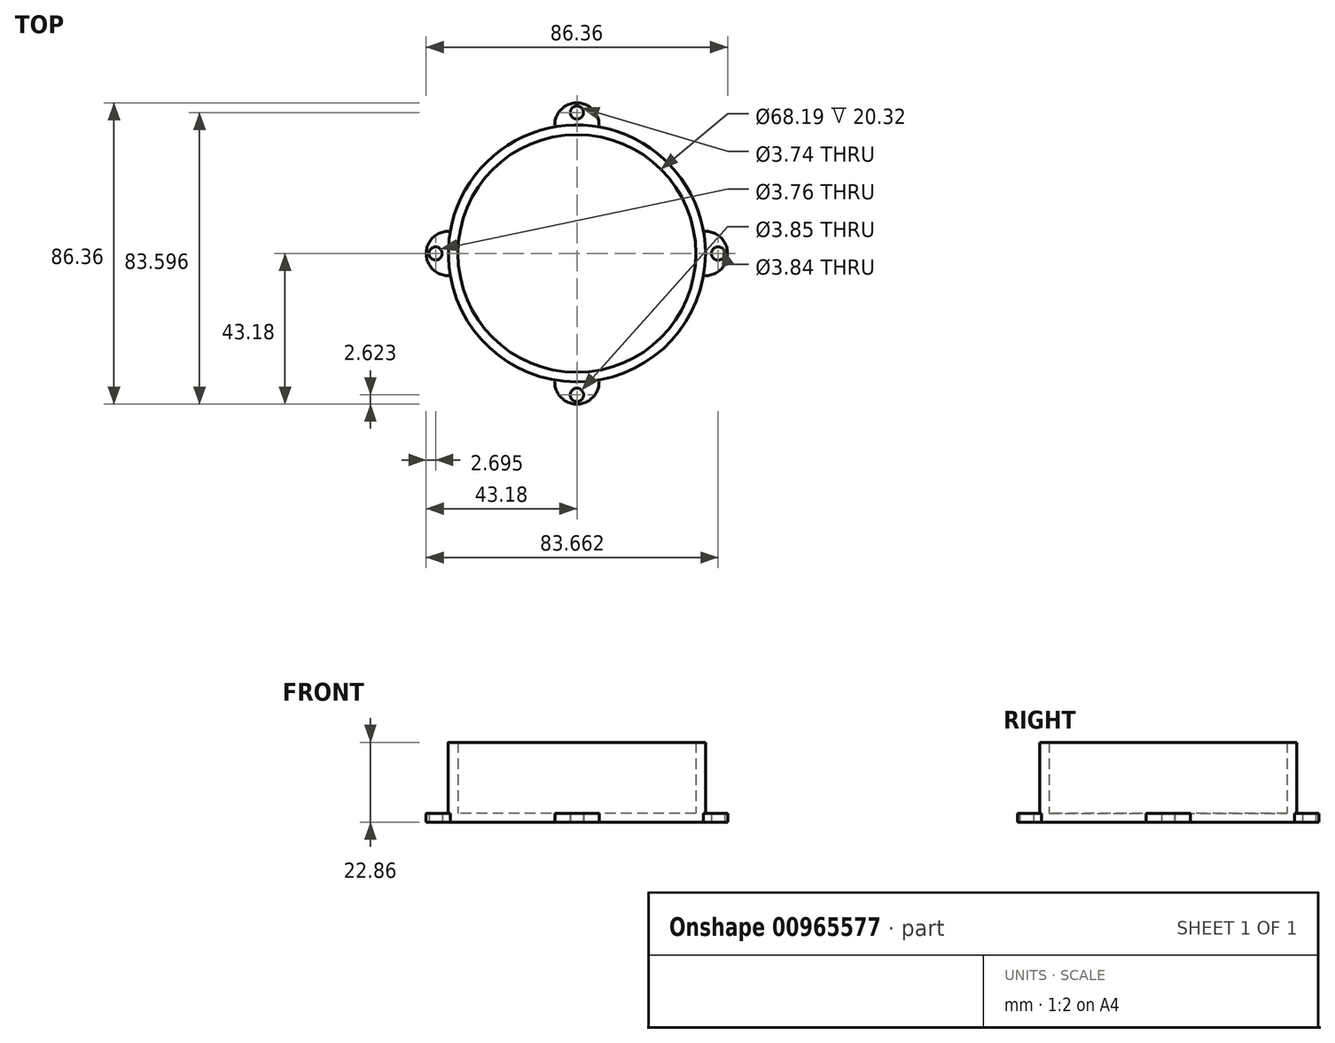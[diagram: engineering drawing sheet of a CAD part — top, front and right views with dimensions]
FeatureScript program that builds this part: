
annotation { "Feature Type Name" : "Feature", "Feature Type Description" : "" }
export const myFeature = defineFeature(function(context is Context, id is Id, definition is map)
    precondition{}
    {
        {
            var Q0;
            Q0=qCreatedBy(makeId("Top.planeOp"),FACE);
            var sketch = newSketch(context, id + "F0", { "sketchPlane" : qUnion([Q0])});
            skCircle(sketch, "E0", {"center": v(0, 0) * mm, "radius": 36.83 * mm});
            skCircle(sketch, "E1", {"center": v(0, 0) * mm, "radius": 34.1 * mm});
            skCircle(sketch, "E2", {"center": v(0, 36.83) * mm, "radius": 6.35 * mm});
            skCircle(sketch, "E3", {"center": v(36.83, 0) * mm, "radius": 6.35 * mm});
            skCircle(sketch, "E4", {"center": v(0, -36.83) * mm, "radius": 6.35 * mm});
            skCircle(sketch, "E5", {"center": v(-36.83, 0) * mm, "radius": 6.35 * mm});
            skCircle(sketch, "E6", {"center": v(0, 40.42) * mm, "radius": 1.87 * mm});
            skCircle(sketch, "E7", {"center": v(40.48, 0) * mm, "radius": 1.92 * mm});
            skCircle(sketch, "E8", {"center": v(-40.48, 0) * mm, "radius": 1.88 * mm});
            skCircle(sketch, "E9", {"center": v(0, -40.56) * mm, "radius": 1.93 * mm});
            skSolve(sketch);
        }
        {
            var Q0;
            {var subQ0=sQuery(id+"F0.wireOp",EDGE,"E2");var subQ1=sQuery(id+"F0.wireOp",EDGE,"E0");var subQ2=makeQuery(id+"F0.imprint","INTERSECT",VERTEX,{"disambiguationData":[OD(0.0)],"derivedFrom":[subQ1,subQ0]});Q0=makeQuery(id+"F0.imprint","IMPRINT",FACE,{"disambiguationData":[TD([[makeQuery(id+"F0.imprint","IMPRINT",EDGE,{"disambiguationData":[TD([[subQ2,1.0]])],"derivedFrom":subQ1}),1.0]])]});}
            var Q1;
            {var subQ0=sQuery(id+"F0.wireOp",EDGE,"E2");var subQ1=sQuery(id+"F0.wireOp",EDGE,"E0");var subQ2=makeQuery(id+"F0.imprint","INTERSECT",VERTEX,{"disambiguationData":[OD(1.0)],"derivedFrom":[subQ1,subQ0]});Q1=makeQuery(id+"F0.imprint","IMPRINT",FACE,{"disambiguationData":[TD([[makeQuery(id+"F0.imprint","IMPRINT",EDGE,{"disambiguationData":[TD([[subQ2,-1.0]])],"derivedFrom":subQ1}),1.0]])]});}
            var Q2;
            {var subQ0=sQuery(id+"F0.wireOp",EDGE,"E5");var subQ1=sQuery(id+"F0.wireOp",EDGE,"E0");var subQ2=makeQuery(id+"F0.imprint","INTERSECT",VERTEX,{"disambiguationData":[OD(1.0)],"derivedFrom":[subQ1,subQ0]});Q2=makeQuery(id+"F0.imprint","IMPRINT",FACE,{"disambiguationData":[TD([[makeQuery(id+"F0.imprint","IMPRINT",EDGE,{"disambiguationData":[TD([[subQ2,-1.0]])],"derivedFrom":subQ1}),1.0]])]});}
            var Q3;
            {var subQ0=sQuery(id+"F0.wireOp",EDGE,"E4");var subQ1=sQuery(id+"F0.wireOp",EDGE,"E0");var subQ2=makeQuery(id+"F0.imprint","INTERSECT",VERTEX,{"disambiguationData":[OD(1.0)],"derivedFrom":[subQ1,subQ0]});Q3=makeQuery(id+"F0.imprint","IMPRINT",FACE,{"disambiguationData":[TD([[makeQuery(id+"F0.imprint","IMPRINT",EDGE,{"disambiguationData":[TD([[subQ2,-1.0]])],"derivedFrom":subQ1}),1.0]])]});}
            var Q4;
            {var subQ0=sQuery(id+"F0.wireOp",EDGE,"E2");var subQ1=sQuery(id+"F0.wireOp",EDGE,"E0");var subQ2=makeQuery(id+"F0.imprint","INTERSECT",VERTEX,{"disambiguationData":[OD(0.0)],"derivedFrom":[subQ1,subQ0]});Q4=makeQuery(id+"F0.imprint","IMPRINT",FACE,{"disambiguationData":[TD([[makeQuery(id+"F0.imprint","IMPRINT",EDGE,{"disambiguationData":[TD([[subQ2,-1.0]])],"derivedFrom":subQ1}),1.0]])]});}
            var Q5;
            {var subQ0=sQuery(id+"F0.wireOp",EDGE,"E5");var subQ1=sQuery(id+"F0.wireOp",EDGE,"E0");var subQ2=makeQuery(id+"F0.imprint","INTERSECT",VERTEX,{"disambiguationData":[OD(0.0)],"derivedFrom":[subQ1,subQ0]});Q5=makeQuery(id+"F0.imprint","IMPRINT",FACE,{"disambiguationData":[TD([[makeQuery(id+"F0.imprint","IMPRINT",EDGE,{"disambiguationData":[TD([[subQ2,-1.0]])],"derivedFrom":subQ1}),1.0]])]});}
            var Q6;
            {var subQ0=sQuery(id+"F0.wireOp",EDGE,"E4");var subQ1=sQuery(id+"F0.wireOp",EDGE,"E0");var subQ2=makeQuery(id+"F0.imprint","INTERSECT",VERTEX,{"disambiguationData":[OD(0.0)],"derivedFrom":[subQ1,subQ0]});Q6=makeQuery(id+"F0.imprint","IMPRINT",FACE,{"disambiguationData":[TD([[makeQuery(id+"F0.imprint","IMPRINT",EDGE,{"disambiguationData":[TD([[subQ2,-1.0]])],"derivedFrom":subQ1}),1.0]])]});}
            var Q7;
            {var subQ0=sQuery(id+"F0.wireOp",EDGE,"E3");var subQ1=sQuery(id+"F0.wireOp",EDGE,"E0");var subQ2=makeQuery(id+"F0.imprint","INTERSECT",VERTEX,{"disambiguationData":[OD(0.0)],"derivedFrom":[subQ1,subQ0]});Q7=makeQuery(id+"F0.imprint","IMPRINT",FACE,{"disambiguationData":[TD([[makeQuery(id+"F0.imprint","IMPRINT",EDGE,{"disambiguationData":[TD([[subQ2,1.0]])],"derivedFrom":subQ1}),1.0]])]});}
            extrude(context, id + "F1", {"entities" : qUnion([Q0, Q1, Q2, Q3, Q4, Q5, Q6, Q7]), "depth" : 22.86 * mm, "offsetDistance" : 25.4 * mm});
        }
        {
            var Q0;
            {var subQ1=sQuery(id+"F0.wireOp",EDGE,"E1");var subQ8=sQuery(id+"F0.wireOp",EDGE,"E2");var subQ12=makeQuery(id+"F0.imprint","INTERSECT",VERTEX,{"disambiguationData":[OD(0.0)],"derivedFrom":[subQ1,subQ8]});Q0=makeQuery(id+"F0.imprint","IMPRINT",FACE,{"disambiguationData":[TD([[makeQuery(id+"F0.imprint","IMPRINT",EDGE,{"disambiguationData":[TD([[subQ12,1.0]])],"derivedFrom":subQ1}),1.0]])]});}
            var Q1;
            {var subQ0=sQuery(id+"F0.wireOp",EDGE,"E2");var subQ1=sQuery(id+"F0.wireOp",EDGE,"E0");var subQ2=makeQuery(id+"F0.imprint","INTERSECT",VERTEX,{"disambiguationData":[OD(0.0)],"derivedFrom":[subQ1,subQ0]});Q1=makeQuery(id+"F0.imprint","IMPRINT",FACE,{"disambiguationData":[TD([[makeQuery(id+"F0.imprint","IMPRINT",EDGE,{"disambiguationData":[TD([[subQ2,-1.0]])],"derivedFrom":subQ1}),-1.0]])]});}
            var Q2;
            {var subQ0=sQuery(id+"F0.wireOp",EDGE,"E2");var subQ1=sQuery(id+"F0.wireOp",EDGE,"E1");var subQ2=makeQuery(id+"F0.imprint","INTERSECT",VERTEX,{"disambiguationData":[OD(0.0)],"derivedFrom":[subQ1,subQ0]});Q2=makeQuery(id+"F0.imprint","IMPRINT",FACE,{"disambiguationData":[TD([[makeQuery(id+"F0.imprint","IMPRINT",EDGE,{"disambiguationData":[TD([[subQ2,-1.0]])],"derivedFrom":subQ1}),1.0]])]});}
            var Q3;
            {var subQ0=sQuery(id+"F0.wireOp",EDGE,"E3");var subQ1=sQuery(id+"F0.wireOp",EDGE,"E0");var subQ2=makeQuery(id+"F0.imprint","INTERSECT",VERTEX,{"disambiguationData":[OD(0.0)],"derivedFrom":[subQ1,subQ0]});Q3=makeQuery(id+"F0.imprint","IMPRINT",FACE,{"disambiguationData":[TD([[makeQuery(id+"F0.imprint","IMPRINT",EDGE,{"disambiguationData":[TD([[subQ2,1.0]])],"derivedFrom":subQ1}),-1.0]])]});}
            var Q4;
            {var subQ0=sQuery(id+"F0.wireOp",EDGE,"E3");var subQ1=sQuery(id+"F0.wireOp",EDGE,"E1");var subQ2=makeQuery(id+"F0.imprint","INTERSECT",VERTEX,{"disambiguationData":[OD(0.0)],"derivedFrom":[subQ1,subQ0]});Q4=makeQuery(id+"F0.imprint","IMPRINT",FACE,{"disambiguationData":[TD([[makeQuery(id+"F0.imprint","IMPRINT",EDGE,{"disambiguationData":[TD([[subQ2,1.0]])],"derivedFrom":subQ1}),1.0]])]});}
            var Q5;
            {var subQ0=sQuery(id+"F0.wireOp",EDGE,"E4");var subQ1=sQuery(id+"F0.wireOp",EDGE,"E0");var subQ2=makeQuery(id+"F0.imprint","INTERSECT",VERTEX,{"disambiguationData":[OD(0.0)],"derivedFrom":[subQ1,subQ0]});Q5=makeQuery(id+"F0.imprint","IMPRINT",FACE,{"disambiguationData":[TD([[makeQuery(id+"F0.imprint","IMPRINT",EDGE,{"disambiguationData":[TD([[subQ2,-1.0]])],"derivedFrom":subQ1}),-1.0]])]});}
            var Q6;
            {var subQ0=sQuery(id+"F0.wireOp",EDGE,"E4");var subQ1=sQuery(id+"F0.wireOp",EDGE,"E1");var subQ2=makeQuery(id+"F0.imprint","INTERSECT",VERTEX,{"disambiguationData":[OD(0.0)],"derivedFrom":[subQ1,subQ0]});Q6=makeQuery(id+"F0.imprint","IMPRINT",FACE,{"disambiguationData":[TD([[makeQuery(id+"F0.imprint","IMPRINT",EDGE,{"disambiguationData":[TD([[subQ2,-1.0]])],"derivedFrom":subQ1}),1.0]])]});}
            var Q7;
            {var subQ0=sQuery(id+"F0.wireOp",EDGE,"E5");var subQ1=sQuery(id+"F0.wireOp",EDGE,"E1");var subQ2=makeQuery(id+"F0.imprint","INTERSECT",VERTEX,{"disambiguationData":[OD(0.0)],"derivedFrom":[subQ1,subQ0]});Q7=makeQuery(id+"F0.imprint","IMPRINT",FACE,{"disambiguationData":[TD([[makeQuery(id+"F0.imprint","IMPRINT",EDGE,{"disambiguationData":[TD([[subQ2,-1.0]])],"derivedFrom":subQ1}),1.0]])]});}
            var Q8;
            {var subQ0=sQuery(id+"F0.wireOp",EDGE,"E5");var subQ1=sQuery(id+"F0.wireOp",EDGE,"E0");var subQ2=makeQuery(id+"F0.imprint","INTERSECT",VERTEX,{"disambiguationData":[OD(0.0)],"derivedFrom":[subQ1,subQ0]});Q8=makeQuery(id+"F0.imprint","IMPRINT",FACE,{"disambiguationData":[TD([[makeQuery(id+"F0.imprint","IMPRINT",EDGE,{"disambiguationData":[TD([[subQ2,-1.0]])],"derivedFrom":subQ1}),-1.0]])]});}
            extrude(context, id + "F2", {"entities" : qUnion([Q0, Q1, Q2, Q3, Q4, Q5, Q6, Q7, Q8]), "operationType" : NewBodyOperationType.ADD, "depth" : 2.54 * mm, "offsetDistance" : 25.4 * mm});
        }
    });
